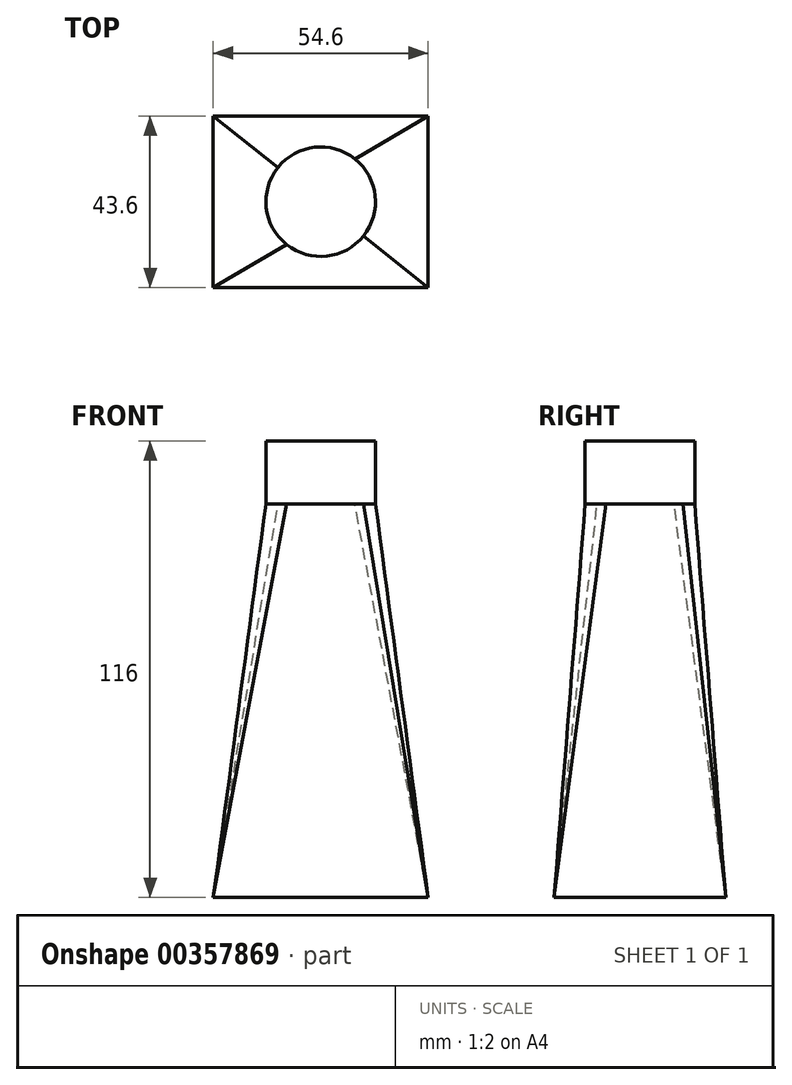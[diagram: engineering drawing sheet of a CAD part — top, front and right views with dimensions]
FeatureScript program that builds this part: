
annotation { "Feature Type Name" : "Feature", "Feature Type Description" : "" }
export const myFeature = defineFeature(function(context is Context, id is Id, definition is map)
    precondition{}
    {
        {
            var Q0;
            Q0=qCreatedBy(makeId("Top.planeOp"),FACE);
            var sketch = newSketch(context, id + "F0", { "sketchPlane" : qUnion([Q0])});
            skLineSegment(sketch, "E0.bottom", {"start": v(27.3, -21.8) * mm, "end": v(-27.3, -21.8) * mm});
            skLineSegment(sketch, "E0.top", {"start": v(27.3, 21.8) * mm, "end": v(-27.3, 21.8) * mm});
            skLineSegment(sketch, "E0.left", {"start": v(27.3, -21.8) * mm, "end": v(27.3, 21.8) * mm});
            skLineSegment(sketch, "E0.right", {"start": v(-27.3, -21.8) * mm, "end": v(-27.3, 21.8) * mm});
            skPoint(sketch, "E0.middle", {"position": v(0, 0) * mm});
            skSolve(sketch);
        }
        {
            var Q0;
            Q0=qCreatedBy(makeId("Top.planeOp"),FACE);
            cPlane(context, id + "F1", {"entities" : qUnion([Q0]), "cplaneType" : CPlaneType.OFFSET, "offset" : 50 * mm, "width" : 152.4 * mm, "height" : 152.4 * mm});
        }
        {
            var Q0;
            Q0=qCreatedBy(id+"F1.planeOp",FACE);
            cPlane(context, id + "F2", {"entities" : qUnion([Q0]), "cplaneType" : CPlaneType.OFFSET, "offset" : 50 * mm, "width" : 150 * mm, "height" : 150 * mm});
        }
        {
            var Q0;
            Q0=qCreatedBy(id+"F2.planeOp",FACE);
            var sketch = newSketch(context, id + "F3", { "sketchPlane" : qUnion([Q0])});
            skCircle(sketch, "E1", {"center": v(0, 0) * mm, "radius": 13.91 * mm});
            skSolve(sketch);
        }
        {
            var Q0;
            Q0=makeQuery(id+"F0.imprint","IMPRINT",FACE,{"disambiguationData":[TD([[makeQuery(id+"F0.imprint","IMPRINT",EDGE,{"derivedFrom":sQuery(id+"F0.wireOp",EDGE,"E0.bottom")}),-1.0]])]});
            var Q1;
            Q1=makeQuery(id+"F3.imprint","IMPRINT",FACE,{"disambiguationData":[TD([[makeQuery(id+"F3.imprint","IMPRINT",EDGE,{"derivedFrom":sQuery(id+"F3.wireOp",EDGE,"E1")}),1.0]])]});
            loft(context, id + "F4", {"sheetProfilesArray" : [{ "sheetProfileEntities" : qUnion([Q0]) }, { "sheetProfileEntities" : qUnion([Q1]) }]});
        }
        {
            var Q0;
            Q0=makeQuery(id+"F4.opLoft","CAP_FACE",FACE,{"disambiguationData":[OSD([makeQuery(id+"F3.imprint","IMPRINT",FACE,{"disambiguationData":[TD([[makeQuery(id+"F3.imprint","IMPRINT",EDGE,{"derivedFrom":sQuery(id+"F3.wireOp",EDGE,"E1")}),1.0]])]})])],"isStart":true});
            extrude(context, id + "F5", {"entities" : qUnion([Q0]), "operationType" : NewBodyOperationType.ADD, "depth" : 16 * mm});
        }
    });
